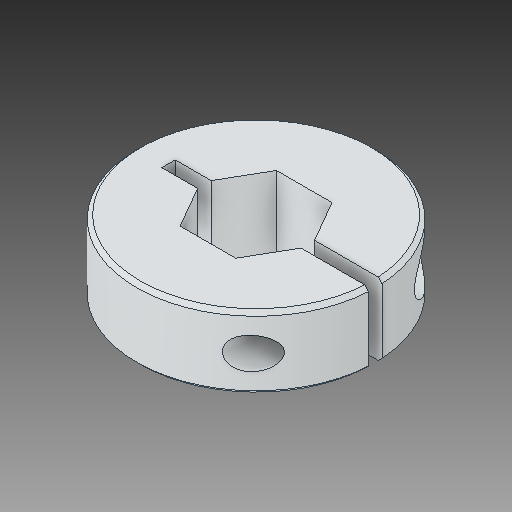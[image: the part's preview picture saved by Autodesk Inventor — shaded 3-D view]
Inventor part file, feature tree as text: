
AUTODESK INVENTOR PART (.ipt)
format: ipt  version: 2017 (Build 210142000, 142)  size: 136,704 bytes
history: native  units: in
note: dims shown in document units (in); Inventor stores cm internally (conversion verified against a paired STEP export)
features: chamfer x1
ambient origin geometry x8: Origin, YZ Plane, XZ Plane, XY Plane, X Axis, Y Axis, Z Axis, Center Point
bodies: Solid1 (feature_tree)
feature tree (1):
  chamfer  "Chamfer1"  [1 undecoded]
note: 1 required parameter value undecoded (feature->parameter linkage not recoverable at this tier; creation-order binding heuristic only, values carry confidence <= 0.55)
